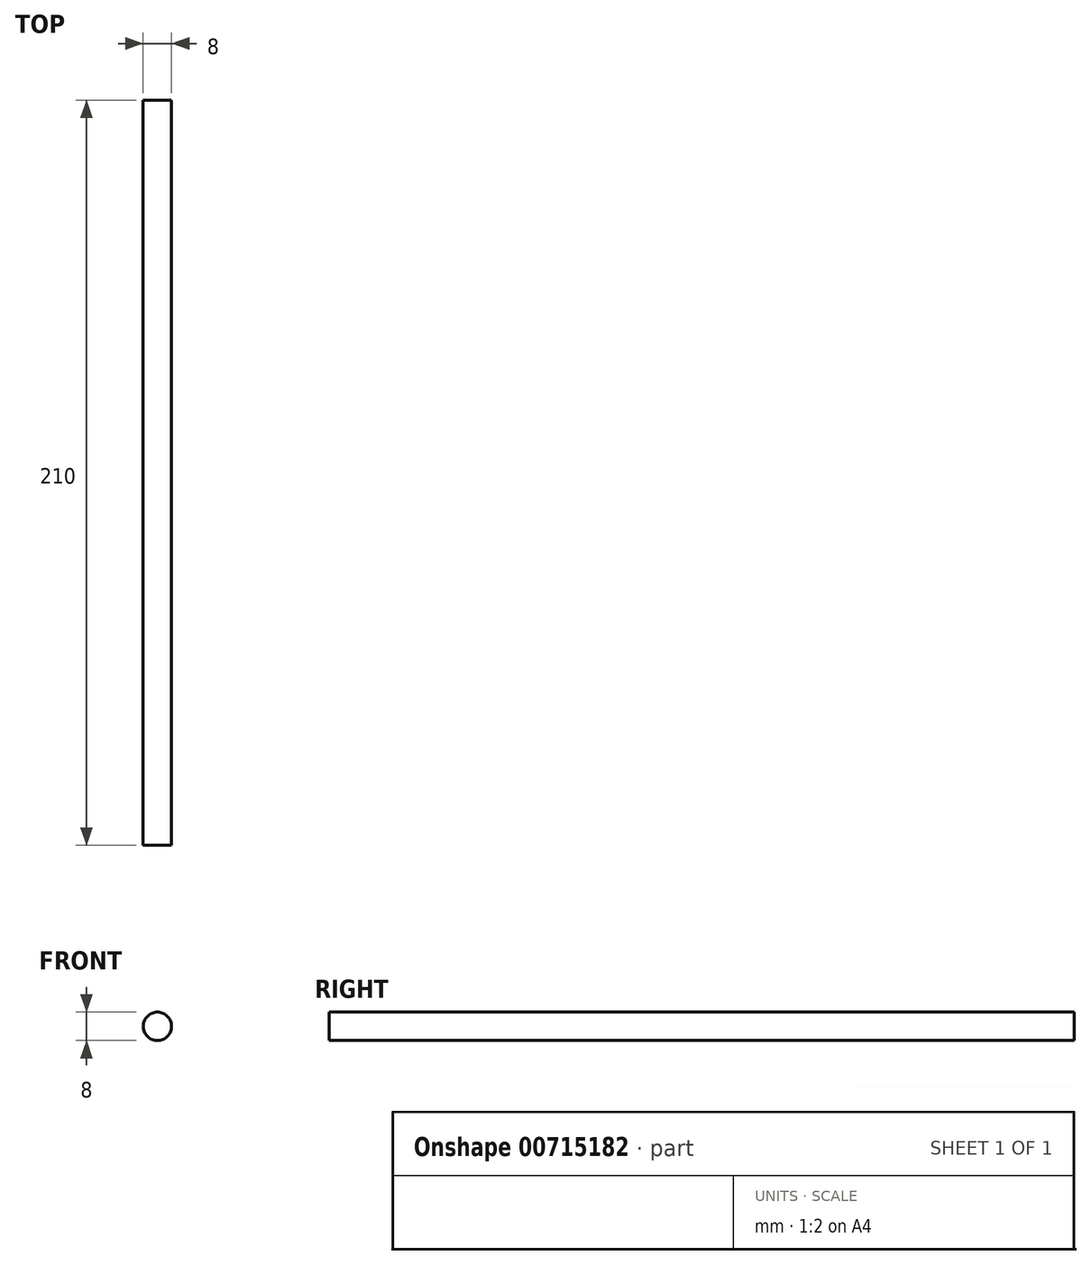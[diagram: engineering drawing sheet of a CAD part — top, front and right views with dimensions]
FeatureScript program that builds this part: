
annotation { "Feature Type Name" : "Feature", "Feature Type Description" : "" }
export const myFeature = defineFeature(function(context is Context, id is Id, definition is map)
    precondition{}
    {
        {
            var Q0;
            Q0=qCreatedBy(makeId("Front.planeOp"),FACE);
            var sketch = newSketch(context, id + "F0", { "sketchPlane" : qUnion([Q0])});
            skCircle(sketch, "E0", {"center": v(0, 0) * mm, "radius": 4 * mm});
            skSolve(sketch);
        }
        {
            var Q0;
            Q0 = qSketchRegion(id + "F0", true);
            extrude(context, id + "F1", {"entities" : qUnion([Q0]), "endBound" : BoundingType.SYMMETRIC, "depth" : 210 * mm, "offsetDistance" : 25 * mm});
        }
    });
